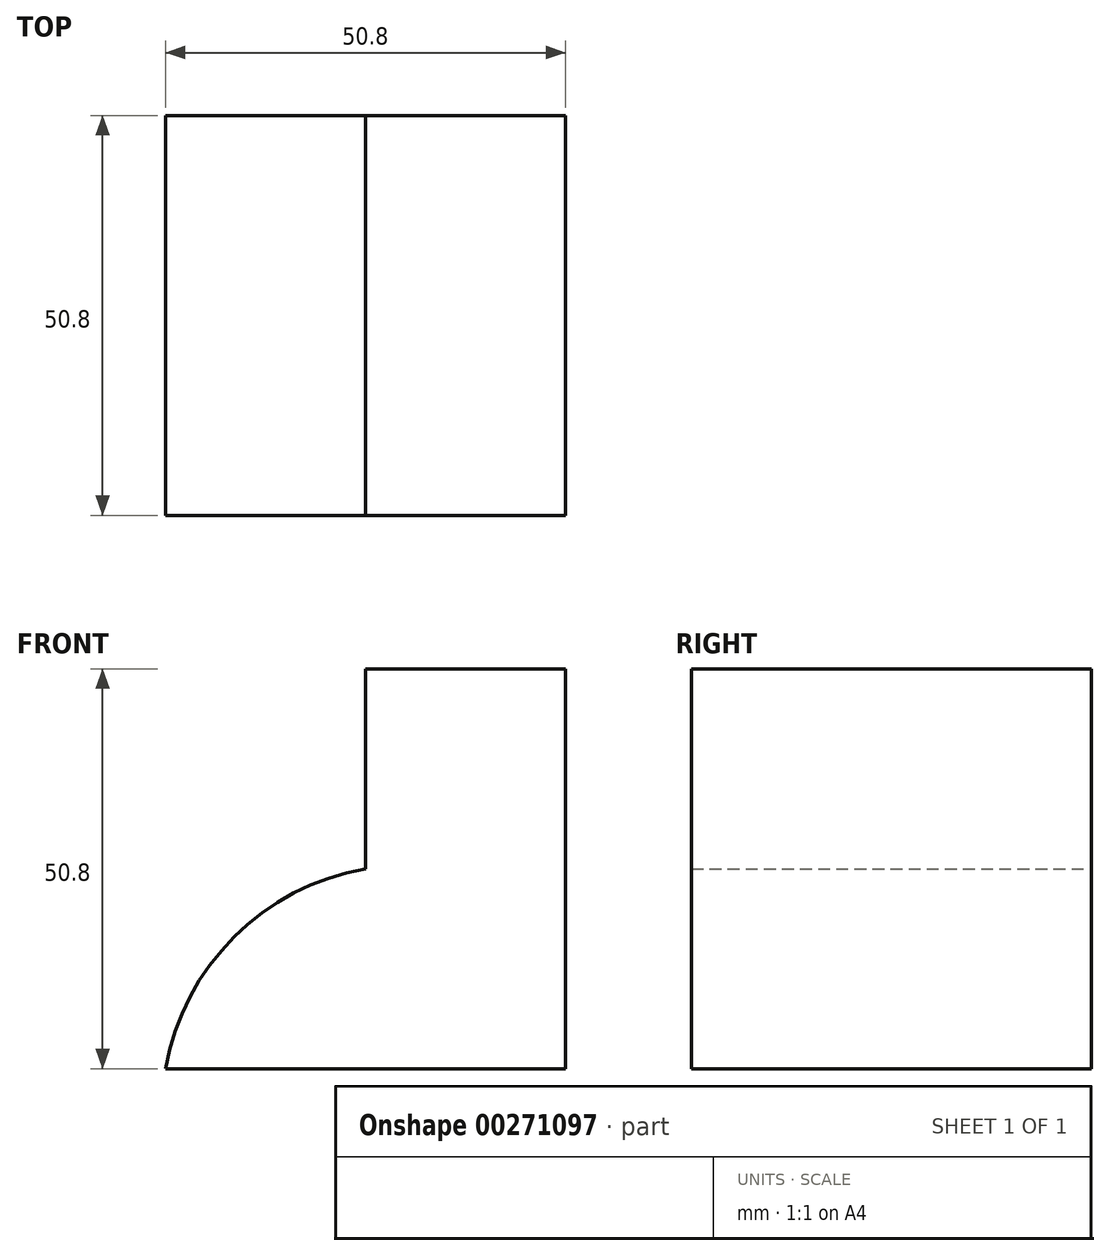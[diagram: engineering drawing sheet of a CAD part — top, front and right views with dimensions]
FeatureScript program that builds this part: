
annotation { "Feature Type Name" : "Feature", "Feature Type Description" : "" }
export const myFeature = defineFeature(function(context is Context, id is Id, definition is map)
    precondition{}
    {
        {
            var Q0;
            Q0=qCreatedBy(makeId("Front.planeOp"),FACE);
            var sketch = newSketch(context, id + "F0", { "sketchPlane" : qUnion([Q0])});
            skLineSegment(sketch, "E0", {"start": v(0, 0) * mm, "end": v(0, 50.8) * mm});
            skLineSegment(sketch, "E1", {"start": v(0, 50.8) * mm, "end": v(-25.4, 50.8) * mm});
            skLineSegment(sketch, "E2", {"start": v(-25.4, 50.8) * mm, "end": v(-25.4, 25.4) * mm});
            skLineSegment(sketch, "E3", {"start": v(-50.8, 0) * mm, "end": v(0, 0) * mm});
            skArc(sketch, "E4", {"start": v(-25.4, 25.4) * mm, "mid": v(-42.12, 16.72) * mm, "end": v(-50.8, 0) * mm});
            skSolve(sketch);
        }
        {
            var Q0;
            Q0 = qSketchRegion(id + "F0", true);
            extrude(context, id + "F1", {"entities" : qUnion([Q0]), "depth" : 50.8 * mm});
        }
    });
